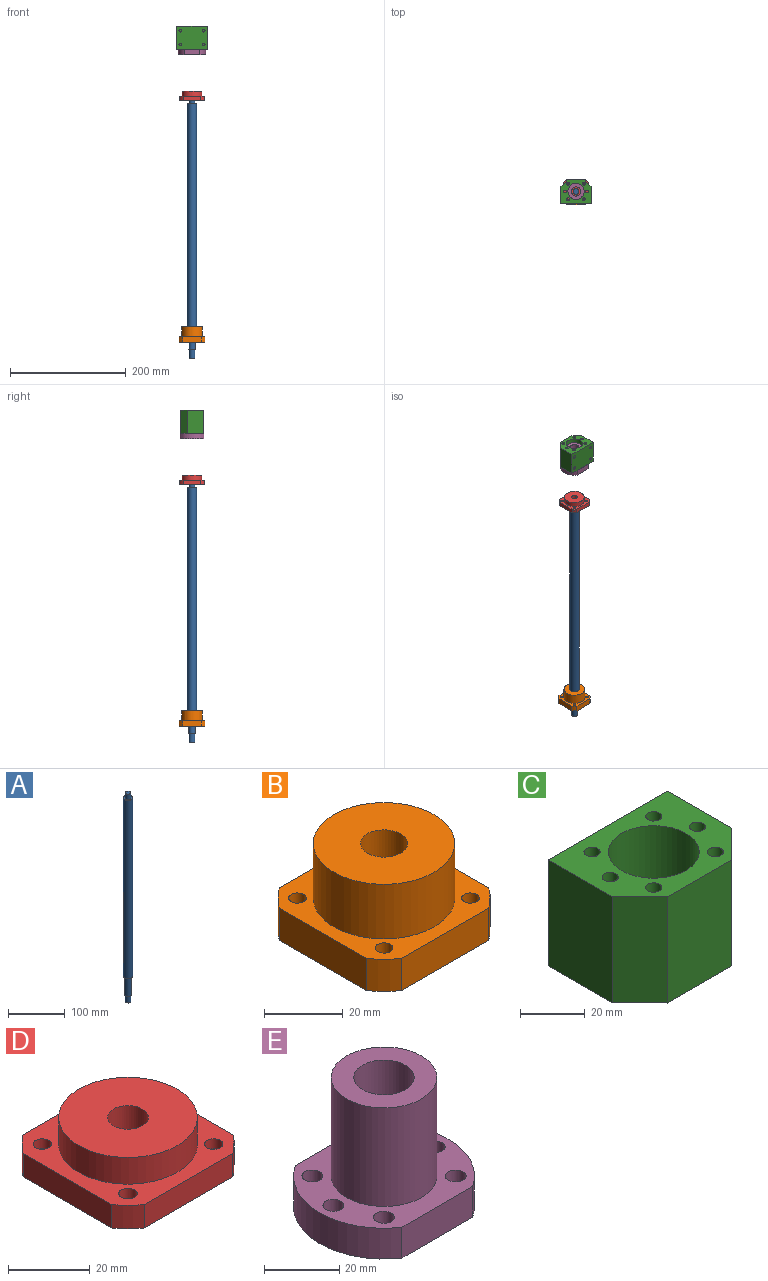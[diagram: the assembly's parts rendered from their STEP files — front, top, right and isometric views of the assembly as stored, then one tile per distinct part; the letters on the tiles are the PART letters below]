
ASSEMBLY  parts=5 mates=6
PART A: 9 faces, bbox 16x16x450 mm
  f0: cylinder r=5mm len=11mm, axis (0,0,-1), area 345.6mm2, adj f1,f2
  f1: plane 10x10mm, normal (0,0,1), area 78.5mm2, adj f0
  f2: plane 16x16mm, normal (0,0,1), area 122.5mm2, adj f0,f4
  f3: plane 16x16mm, normal (0,0,-1), area 88mm2, adj f4,f5
  f4: cylinder r=8mm len=385mm, axis (0,0,-1), area 19352.2mm2, adj f2,f3
  f5: cylinder r=6mm len=39mm, axis (0,0,-1), area 1470.3mm2, adj f3,f6
  f6: plane 12x12mm, normal (0,0,-1), area 34.6mm2, adj f5,f8
  f7: plane 10x10mm, normal (0,0,-1), area 78.5mm2, adj f8
  f8: cylinder r=5mm len=15mm, axis (0,0,-1), area 471.2mm2, adj f6,f7
PART B: 25 faces, bbox 44x44x27 mm
  f0: cylinder r=4mm len=8mm, axis (0,0,-1), area 100.5mm2, adj f14,f22
  f1: cylinder r=4mm len=8mm, axis (0,0,-1), area 100.5mm2, adj f14,f20
  f2: cylinder r=4mm len=8mm, axis (0,0,-1), area 100.5mm2, adj f14,f18
  f3: cylinder r=4mm len=8mm, axis (0,0,-1), area 100.5mm2, adj f14,f16
  f4: plane 31.31x10mm, normal (1,0,0), area 313mm2, adj f5,f11,f13,f14
  f5: cylinder r=27mm len=10mm, axis (0,0,-1), area 90.2mm2, adj f4,f6,f13,f14
  f6: plane 31.31x10mm, normal (0,1,0), area 313mm2, adj f5,f7,f13,f14
  f7: cylinder r=27mm len=10mm, axis (0,0,-1), area 90.2mm2, adj f6,f8,f13,f14
  f8: plane 31.31x10mm, normal (-1,0,0), area 313mm2, adj f7,f9,f13,f14
  f9: cylinder r=27mm len=10mm, axis (0,0,-1), area 90.2mm2, adj f8,f10,f13,f14
  f10: plane 31.31x10mm, normal (0,-1,0), area 313mm2, adj f9,f11,f13,f14
  f11: cylinder r=27mm len=10mm, axis (0,0,-1), area 90.2mm2, adj f4,f10,f13,f14
  f12: cylinder r=6mm len=27mm, axis (0,0,-1), area 1017.9mm2, adj f14,f24
  f13: plane 44x44mm, normal (0,0,1), area 782.9mm2, adj f4,f5,f6,f7,f8,f9,f10,f11
  f14: plane 44x44mm, normal (0,0,-1), area 1550.3mm2, adj f0,f1,f2,f3,f4,f5,f6,f7
  f15: cylinder r=2.25mm len=6mm, axis (0,0,-1), area 84.8mm2, adj f13,f16
  f16: plane 8x8mm, normal (0,0,-1), area 34.4mm2, adj f3,f15
  f17: cylinder r=2.25mm len=6mm, axis (0,0,-1), area 84.8mm2, adj f13,f18
  f18: plane 8x8mm, normal (0,0,-1), area 34.4mm2, adj f2,f17
  f19: cylinder r=2.25mm len=6mm, axis (0,0,-1), area 84.8mm2, adj f13,f20
  f20: plane 8x8mm, normal (0,0,-1), area 34.4mm2, adj f1,f19
  f21: cylinder r=2.25mm len=6mm, axis (0,0,-1), area 84.8mm2, adj f13,f22
  f22: plane 8x8mm, normal (0,0,-1), area 34.4mm2, adj f0,f21
  f23: cylinder r=18mm len=36mm, axis (0,0,-1), area 1922.7mm2, adj f13,f24
  f24: plane 36x36mm, normal (0,0,1), area 904.8mm2, adj f12,f23
PART C: 23 faces, bbox 52x40x40 mm
  f0: plane 52x40mm, normal (0,1,0), area 2001.5mm2, adj f1,f11,f13,f14,f15,f17,f19,f21
  f1: plane 40x28mm, normal (-1,0,0), area 1120mm2, adj f0,f2,f13,f14
  f2: plane 40x12mm, normal (-0.71,-0.71,0), area 678.8mm2, adj f1,f3,f13,f14
  f3: plane 40x28mm, normal (0,-1,0), area 1120mm2, adj f2,f4,f13,f14
  f4: plane 40x12mm, normal (0.71,-0.71,0), area 678.8mm2, adj f3,f11,f13,f14
  f5: cylinder r=2.5mm len=40mm, axis (0,0,-1), area 628.3mm2, adj f13,f14
  f6: cylinder r=2.5mm len=40mm, axis (0,0,-1), area 628.3mm2, adj f13,f14
  f7: cylinder r=2.5mm len=40mm, axis (0,0,-1), area 628.3mm2, adj f13,f14
  f8: cylinder r=2.5mm len=40mm, axis (0,0,-1), area 628.3mm2, adj f13,f14
  f9: cylinder r=2.5mm len=40mm, axis (0,0,-1), area 628.3mm2, adj f13,f14
  f10: cylinder r=14mm len=40mm, axis (0,0,-1), area 3518.6mm2, adj f13,f14
  f11: plane 40x28mm, normal (1,0,0), area 1120mm2, adj f0,f4,f13,f14
  f12: cylinder r=2.5mm len=40mm, axis (0,0,-1), area 628.3mm2, adj f13,f14
  f13: plane 52x40mm, normal (0,0,1), area 1202.4mm2, adj f0,f1,f2,f3,f4,f5,f6,f7
  f14: plane 52x40mm, normal (0,0,-1), area 1202.4mm2, adj f0,f1,f2,f3,f4,f5,f6,f7
  f15: cylinder r=2.5mm len=15mm, axis (0,1,0), area 235.6mm2, adj f0,f16
  f16: plane 5x5mm, normal (0,1,0), area 19.6mm2, adj f15
  f17: cylinder r=2.5mm len=15mm, axis (0,1,0), area 235.6mm2, adj f0,f18
  f18: plane 5x5mm, normal (0,1,0), area 19.6mm2, adj f17
  f19: cylinder r=2.5mm len=15mm, axis (0,1,0), area 235.6mm2, adj f0,f20
  f20: plane 5x5mm, normal (0,1,0), area 19.6mm2, adj f19
  f21: cylinder r=2.5mm len=15mm, axis (0,1,0), area 235.6mm2, adj f0,f22
  f22: plane 5x5mm, normal (0,1,0), area 19.6mm2, adj f21
PART D: 25 faces, bbox 42x42x15 mm
  f0: cylinder r=4mm len=8mm, axis (0,0,-1), area 100.5mm2, adj f14,f22
  f1: cylinder r=4mm len=8mm, axis (0,0,-1), area 100.5mm2, adj f14,f20
  f2: cylinder r=4mm len=8mm, axis (0,0,-1), area 100.5mm2, adj f14,f18
  f3: cylinder r=4mm len=8mm, axis (0,0,-1), area 100.5mm2, adj f14,f16
  f4: plane 30.66x7mm, normal (1,0,0), area 214.6mm2, adj f5,f11,f13,f14
  f5: cylinder r=26mm len=7mm, axis (0,0,-1), area 56.4mm2, adj f4,f6,f13,f14
  f6: plane 30.66x7mm, normal (0,1,0), area 214.6mm2, adj f5,f7,f13,f14
  f7: cylinder r=26mm len=7mm, axis (0,0,-1), area 56.4mm2, adj f6,f8,f13,f14
  f8: plane 30.66x7mm, normal (-1,0,0), area 214.6mm2, adj f7,f9,f13,f14
  f9: cylinder r=26mm len=7mm, axis (0,0,-1), area 56.4mm2, adj f8,f10,f13,f14
  f10: plane 30.66x7mm, normal (0,-1,0), area 214.6mm2, adj f9,f11,f13,f14
  f11: cylinder r=26mm len=7mm, axis (0,0,-1), area 56.4mm2, adj f4,f10,f13,f14
  f12: cylinder r=5mm len=15mm, axis (0,0,-1), area 471.2mm2, adj f14,f24
  f13: plane 42x42mm, normal (0,0,1), area 734.8mm2, adj f4,f5,f6,f7,f8,f9,f10,f11
  f14: plane 42x42mm, normal (0,0,-1), area 1426.8mm2, adj f0,f1,f2,f3,f4,f5,f6,f7
  f15: cylinder r=2.25mm len=4.5mm, axis (0,0,-1), area 42.4mm2, adj f13,f16
  f16: plane 8x8mm, normal (0,0,-1), area 34.4mm2, adj f3,f15
  f17: cylinder r=2.25mm len=4.5mm, axis (0,0,-1), area 42.4mm2, adj f13,f18
  f18: plane 8x8mm, normal (0,0,-1), area 34.4mm2, adj f2,f17
  f19: cylinder r=2.25mm len=4.5mm, axis (0,0,-1), area 42.4mm2, adj f13,f20
  f20: plane 8x8mm, normal (0,0,-1), area 34.4mm2, adj f1,f19
  f21: cylinder r=2.25mm len=4.5mm, axis (0,0,-1), area 42.4mm2, adj f13,f22
  f22: plane 8x8mm, normal (0,0,-1), area 34.4mm2, adj f0,f21
  f23: cylinder r=17mm len=34mm, axis (0,0,-1), area 854.5mm2, adj f13,f24
  f24: plane 34x34mm, normal (0,0,1), area 829.4mm2, adj f12,f23
PART E: 15 faces, bbox 48x40x42 mm
  f0: plane 26.53x10mm, normal (0,1,0), area 265.3mm2, adj f1,f3,f11,f12
  f1: cylinder r=24mm len=40mm, axis (0,0,-1), area 472.9mm2, adj f0,f2,f11,f12
  f2: plane 26.53x10mm, normal (0,-1,0), area 265.3mm2, adj f1,f3,f11,f12
  f3: cylinder r=24mm len=40mm, axis (0,0,-1), area 472.9mm2, adj f0,f2,f11,f12
  f4: cylinder r=2.75mm len=10mm, axis (0,0,-1), area 172.8mm2, adj f11,f12
  f5: cylinder r=2.75mm len=10mm, axis (0,0,-1), area 172.8mm2, adj f11,f12
  f6: cylinder r=2.75mm len=10mm, axis (0,0,-1), area 172.8mm2, adj f11,f12
  f7: cylinder r=2.75mm len=10mm, axis (0,0,-1), area 172.8mm2, adj f11,f12
  f8: cylinder r=2.75mm len=10mm, axis (0,0,-1), area 172.8mm2, adj f11,f12
  f9: cylinder r=2.75mm len=10mm, axis (0,0,-1), area 172.8mm2, adj f11,f12
  f10: cylinder r=8mm len=42mm, axis (0,0,-1), area 2111.2mm2, adj f12,f14
  f11: plane 48x40mm, normal (0,0,1), area 907.2mm2, adj f0,f1,f2,f3,f4,f5,f6,f7
  f12: plane 48x40mm, normal (0,0,-1), area 1321.9mm2, adj f0,f1,f2,f3,f4,f5,f6,f7
  f13: cylinder r=14mm len=32mm, axis (0,0,-1), area 2814.9mm2, adj f11,f14
  f14: plane 28x28mm, normal (0,0,1), area 414.7mm2, adj f10,f13
PLACE A t=(-2.27,-0.45,960.2)mm
PLACE B t=(-15.4,-246.76,987.2)mm
PLACE C rot(axis=(1,0,0),180deg) t=(-120.9,55.75,1533)mm
PLACE D t=(-105.01,-247.6,1405.2)mm
PLACE E t=(-19.88,74.23,1483)mm
MATE parallel D.f10 <-> B.f10  axis (0,-1,0) through (-51.13,13.99,1408.7)mm
MATE cylindrical D.f5 <-> A.f0  axis (0,0,-1) through (-51.13,34.99,1412.7)mm
MATE parallel D.f5 <-> A.f0  axis (0,0,-1) through (-51.13,34.99,1405.2)mm
MATE planar B.f5 <-> A.f0  axis (0,0,1) through (-51.13,34.99,1014.2)mm
MATE cylindrical E.f1 <-> A.f0  axis (0,0,-1) through (-51.13,34.99,1504)mm
MATE cylindrical B.f5 <-> A.f0  axis (0,0,-1) through (-51.13,34.99,1014.2)mm
